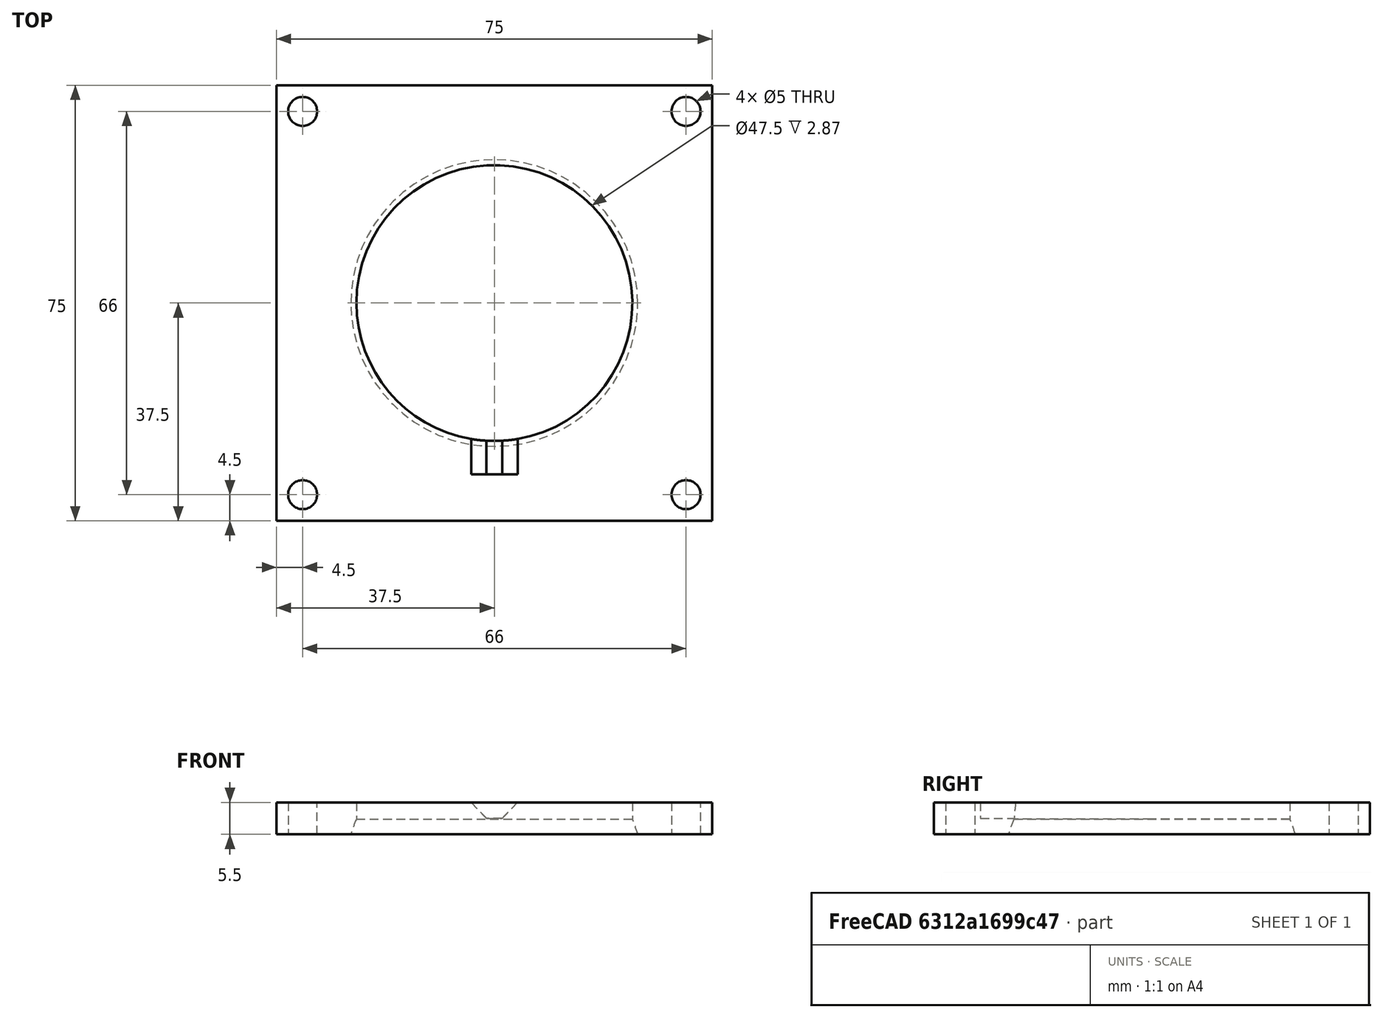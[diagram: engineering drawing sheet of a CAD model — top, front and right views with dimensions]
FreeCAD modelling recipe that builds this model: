
FCSTD DOCUMENT  (FreeCAD 0.18R16110 (Git))
Label: newhubbase
License: All rights reserved
LicenseURL: http://en.wikipedia.org/wiki/All_rights_reserved
objects: Sketcher::SketchObject×3, Mesh::Feature×3, Part::Extrusion×2, Part::Cut×2, Part::Revolution×1
note: 8 computed .brp shape members not serialized (recipe doc carries the construction recipe); baked Part::Feature solids carry a one-line shape summary decoded from their .brp

FEATURE [Sketcher::SketchObject] Sketch
  Placement = pos=(0,0,-12.5) rot=(0,0,1;0rad)
  sketch-geometry (10):
    g0: LineSegment StartX=-37.5 StartY=37.5 StartZ=0 EndX=37.5 EndY=37.5 EndZ=0
    g1: LineSegment StartX=37.5 StartY=37.5 StartZ=0 EndX=37.5 EndY=-37.5 EndZ=0
    g2: LineSegment StartX=37.5 StartY=-37.5 StartZ=0 EndX=-37.5 EndY=-37.5 EndZ=0
    g3: LineSegment StartX=-37.5 StartY=-37.5 StartZ=0 EndX=-37.5 EndY=37.5 EndZ=0
    g4: Circle CenterX=-33 CenterY=33 CenterZ=0 NormalX=0 NormalY=0 NormalZ=1 AngleXU=0 Radius=2.5
    g5: Circle CenterX=33 CenterY=33 CenterZ=0 NormalX=0 NormalY=0 NormalZ=1 AngleXU=0 Radius=2.5
    g6: Circle CenterX=-33 CenterY=-33 CenterZ=0 NormalX=0 NormalY=0 NormalZ=1 AngleXU=0 Radius=2.5
    g7: Circle CenterX=33 CenterY=-33 CenterZ=0 NormalX=0 NormalY=0 NormalZ=1 AngleXU=0 Radius=2.5
    g8: LineSegment [constr] StartX=33 StartY=37.5 StartZ=0 EndX=33 EndY=35.5 EndZ=0
    g9: LineSegment [constr] StartX=35.5 StartY=33 StartZ=0 EndX=37.5 EndY=33 EndZ=0
  constraints (27):
    c: Coincident(g0,g1)
    c: Coincident(g1,g2)
    c: Coincident(g2,g3)
    c: Coincident(g3,g0)
    c: Horizontal(g2)
    c: Vertical(g1)
    c: Symmetric(g0,g0,g-2)
    c: Symmetric(g0,g2,g-1)
    c: Distance(g0) = 75
    c: Distance(g3) = 75
    c: Symmetric(g4,g5,g-2)
    c: Symmetric(g6,g4,g-1)
    c: Symmetric(g7,g6,g-2)
    c: Radius(g5) = 2.5
    c: Radius(g4) = 2.5
    c: Radius(g6) = 2.5
    c: Radius(g7) = 2.5
    c: PointOnObject(g8,g0)
    c: PointOnObject(g8,g5)
    c: Vertical(g8)
    c: Distance(g8) = 2
    c: PointOnObject(g9,g5)
    c: PointOnObject(g9,g1)
    c: Horizontal(g9)
    c: Distance(g9) = 2
    c: Perpendicular(g5,g9)
    c: Perpendicular(g5,g8)
FEATURE [Part::Extrusion] Extrude
  Base = -> Sketch
  Dir = (0,0,1)
  DirMode = 2
  FaceMakerClass = Part::FaceMakerBullseye
  LengthFwd = 5.5
  LengthRev = 0
  Solid = true
  Symmetric = false
FEATURE [Sketcher::SketchObject] Sketch001
  MapMode = 3
  Placement = pos=(0,0,-12.5) rot=(1,0,0;1.5708rad)
  Support = -> [Sketch]
  sketch-geometry (5):
    g0: LineSegment StartX=0 StartY=5.5 StartZ=0 EndX=-23.75 EndY=5.5 EndZ=0
    g1: LineSegment StartX=-23.75 StartY=5.5 StartZ=0 EndX=-23.75 EndY=2.63 EndZ=0
    g2: LineSegment StartX=-24.6877 StartY=-1.42e-14 StartZ=0 EndX=0 EndY=0 EndZ=0
    g3: LineSegment StartX=0 StartY=0 StartZ=0 EndX=0 EndY=5.5 EndZ=0
    g4: ArcOfCircle CenterX=0 CenterY=-7.31987 CenterZ=0 NormalX=0 NormalY=0 NormalZ=1 AngleXU=0 Radius=25.75 StartAngle=2.74486 EndAngle=2.85335
  constraints (15):
    c: PointOnObject(g0,g-2)
    c: Horizontal(g0)
    c: Coincident(g0,g1)
    c: Vertical(g1)
    c: PointOnObject(g2,g-1)
    c: Coincident(g2,g-1)
    c: Coincident(g2,g3)
    c: Coincident(g3,g0)
    c: DistanceY(g3,g3) = 5.5
    c: DistanceX(g0,g0) = 23.75
    c: DistanceY(g1,g1) = 2.87
    c: PointOnObject(g4,g-2)
    c: Coincident(g4,g2)
    c: Coincident(g4,g1)
    c: Radius(g4) = 25.75
FEATURE [Part::Revolution] Revolve
  Angle = 360
  Axis = (0,0,1)
  Base = (0,0,0)
  FaceMakerClass = Part::FaceMakerBullseye
  Solid = true
  Source = -> Sketch001
  Symmetric = false
FEATURE [Part::Cut] Cut
  Base = -> Extrude
  Tool = -> Revolve
FEATURE [Sketcher::SketchObject] Sketch002
  MapMode = 5
  Placement = pos=(0,-37.5,0) rot=(1,0,0;1.5708rad)
  Support = -> [Cut]
  sketch-geometry (5):
    g0: LineSegment StartX=-4 StartY=-10 StartZ=0 EndX=4 EndY=-10 EndZ=0
    g1: LineSegment StartX=4 StartY=-10 StartZ=0 EndX=1.34436 EndY=-7.25 EndZ=0
    g2: LineSegment StartX=1.34436 StartY=-7.25 StartZ=0 EndX=-1.34436 EndY=-7.25 EndZ=0
    g3: LineSegment StartX=-1.34436 StartY=-7.25 StartZ=0 EndX=-4 EndY=-10 EndZ=0
    g4: LineSegment [constr] StartX=1.34436 StartY=-7.25 StartZ=0 EndX=1.34436 EndY=-10 EndZ=0
  constraints (14):
    c: Coincident(g0,g1)
    c: Coincident(g1,g2)
    c: Horizontal(g2)
    c: Coincident(g2,g3)
    c: Coincident(g3,g0)
    c: Angle(g0,g3) = 0.802851
    c: Angle(g1,g0) = 0.802851
    c: Symmetric(g0,g0,g-2)
    c: DistanceX(g0,g0) = 8
    c: Coincident(g4,g1)
    c: PointOnObject(g4,g0)
    c: Vertical(g4)
    c: DistanceY(g4,g4) = 2.75
    c: DistanceY(g0) = -10
FEATURE [Part::Extrusion] Extrude002
  Base = -> Sketch002
  Dir = (0,-1,2e-16)
  DirMode = 2
  FaceMakerClass = Part::FaceMakerBullseye
  LengthFwd = 8
  LengthRev = 0
  Placement = pos=(0,8,-17) rot=(0,1,0;3.14159rad)
  Reversed = true
  Solid = true
  Symmetric = false
FEATURE [Mesh::Feature] square2_4  label="square2.4"
  Placement = pos=(0.35,39.8,-14) rot=(1,0,0;1.5708rad)
FEATURE [Mesh::Feature] handlecurve
  Placement = pos=(1.9,31,-13) rot=(0.57735,0.57735,-0.57735;4.18879rad)
FEATURE [Mesh::Feature] square2_4001  label="square2.005"
  Placement = pos=(0.35,42,-14) rot=(1,0,0;1.5708rad)
FEATURE [Part::Cut] Cut001
  Base = -> Cut
  Tool = -> Extrude002
